# Revit family: Дио
name_source: partatom
category: Осветительные приборы
units: mm (PartAtom-declared; Revit-internal decimal feet)

## family parameters
Всегда вертикально = Да
Источник света = Да
На основе рабочей плоскости = Нет
Общий = Нет
При загрузке вырезать с полостями = Нет
Размер круглого соединителя = Использовать диаметр
Тип детали = Нормальный
Точка расчета площади = Нет

## types (8) — shared parameters
ADSK_URL страницы изделия = https://www.allfresco.ru
ADSK_Единица измерения = шт.
ADSK_Завод-изготовитель = ALFRESCO
ADSK_Количество фаз = 2
ADSK_Модель = Дио ДТУ-90-AF
ADSK_Напряжение = 220 В
ADSK_Полная мощность = 0 В·А
ADSK_Ток = 0 А
ADSK_Энергоэффективность = 110 лм/Вт
Angle = 45.00°
H_дверка = 860 мм
H_конечной точки = 1500 мм
H_фланец = 8 мм
IP Class = IP 67
L_отступ до конечной точки = 1500 мм
L_отступ до центра = 1000 мм
R_поворот столба = 95 мм
Блок аварийного питания = Нет
Излучение по ширине линии = 610 мм
Класс защиты = 1
Класс пожароопасности = F (светильники предназначены для установки непосредственно на поверхность из нормально воспламеняемых материалов)
Климатическая зона = УХЛ1
Короб_Диаметр = 20 мм
Корпус светильника = Антрацит
Материал рассеивателя = Светотехнический ПК
Область использования = Парки, скверы, общественные пространства, городская инфраструктура
Полная установленная мощность = 0 В·А
Рассеиватель = Белый_светодиод
Светофильтр = 16777215
Смещение цветовой температуры при затухании лампы = <Нет>
Таблица выбора = Таблица параметров светильников_par2
Температура эксплуатации = -40 +50
Тип ИС = LED-модуль
Тип КСС = тип ШБ (широкая боковая)
Тип ПРА = -
Тип продукции = LED-светильник
Угол наклона = 90.00°
Цветоывая температура = 2700-5500
zero-valued in all types: ADSK_Количество фаз числовое, ADSK_Коэффициент мощности

## per-type parameters (varying)
| type | ADSK_Артикул | ADSK_Масса | ADSK_Масса_Текст | ADSK_Наименование | ADSK_Номинальная мощность | ADSK_Размер_Высота | ADSK_Фактическая мощность | D_столб | H_столб | H_точки освещения | L_поворот | R_поворот | R_столб | a_отступ точки освещения | Поворот_Светильники_1 | Понижение | Светильники_2 | Файл фотометрической сетки | Фланец_250 | Фланец_350 |
| ДТУ907 Светодиодный светильник Дио ДТУ-90-AF-40Вт-4,0 | ДТУ907 | 43 | 43 | ДТУ907 Светодиодный светильник Дио ДТУ-90-AF-40Вт-4.0 | 40 Вт | 4000 мм | 38 Вт | 114 мм | 3495 мм | 277 мм | 209 мм | 152 мм | 57 мм | 292 мм | Да | 505 мм | Нет | DTU-90-AF Dio 40W 146x60.ies | Да | Нет |
| ДТУ908 Светодиодный светильник Дио ДТУ-90-AF-80Вт-4,0-2 | ДТУ908 | 48 | 48 | ДТУ908 Светодиодный светильник Дио ДТУ-90-AF-80Вт-4.0-2 | 80 Вт | 4000 мм | 76 Вт | 114 мм | 3495 мм | 277 мм | 209 мм | 152 мм | 57 мм | 292 мм | Нет | 505 мм | Да | DTU-90-AF Dio 60W 146x60.ies | Да | Нет |
| ДТУ9022 Светодиодный светильник Дио ДТУ-90-AF-60Вт-5,0 | ДТУ9022 | 53 | 53 | ДТУ9022 Светодиодный светильник Дио ДТУ-90-AF-60Вт-5.0 | 60 Вт | 5000 мм | 58 Вт | 114 мм | 4495 мм | 277 мм | 209 мм | 152 мм | 57 мм | 292 мм | Да | 505 мм | Нет | DTU-90-AF Dio 60W 146x60.ies | Да | Нет |
| ДТУ9023 Светодиодный светильник Дио ДТУ-90-AF-120Вт-5,0-2 | ДТУ9023 | 58 | 58 | ДТУ9023 Светодиодный светильник Дио ДТУ-90-AF-120Вт-5.0-2 | 120 Вт | 5000 мм | 116 Вт | 114 мм | 4495 мм | 277 мм | 209 мм | 152 мм | 57 мм | 292 мм | Нет | 505 мм | Да | DTU-90-AF Dio 100W 146x60.ies | Да | Нет |
| ДТУ909 Светодиодный светильник Дио ДТУ-90-AF-60Вт-6,0 | ДТУ909 | 62 | 62 | ДТУ909 Светодиодный светильник Дио ДТУ-90-AF-60Вт-6.0 | 60 Вт | 6000 мм | 58 Вт | 114 мм | 5495 мм | 277 мм | 209 мм | 152 мм | 57 мм | 292 мм | Да | 505 мм | Нет | DTU-90-AF Dio 60W 146x60.ies | Да | Нет |
| ДТУ9010 Светодиодный светильник Дио ДТУ-90-AF-120Вт-6,0-2 | ДТУ9010 | 67 | 67 | ДТУ9010 Светодиодный светильник Дио ДТУ-90-AF-120Вт-6.0-2 | 120 Вт | 6000 мм | 116 Вт | 114 мм | 5495 мм | 277 мм | 209 мм | 152 мм | 57 мм | 292 мм | Нет | 505 мм | Да | DTU-90-AF Dio 100W 146x60.ies | Да | Нет |
| ДТУ903 Светодиодный светильник Дио ДТУ-90-AF-100Вт-6,0 | ДТУ903 | 70 | 70 | ДТУ903 Светодиодный светильник Дио ДТУ-90-AF-100Вт-6.0 | 100 Вт | 6000 мм | 98 Вт | 133 мм | 5305 мм | 400 мм | 257 мм | 190 мм | 67 мм | 400 мм | Да | 695 мм | Нет | DTU-90-AF Dio 100W 146x60.ies | Нет | Да |
| ДТУ904 Светодиодный светильник Дио ДТУ-90-AF-200Вт-6,0-2 | ДТУ904 | 75 | 75 | ДТУ904 Светодиодный светильник Дио ДТУ-90-AF-200Вт-6.0-2 | 200 Вт | 6000 мм | 196 Вт | 133 мм | 5305 мм | 400 мм | 257 мм | 190 мм | 67 мм | 400 мм | Нет | 695 мм | Да | DTU-90-AF Dio 100W 146x60.ies | Нет | Да |
